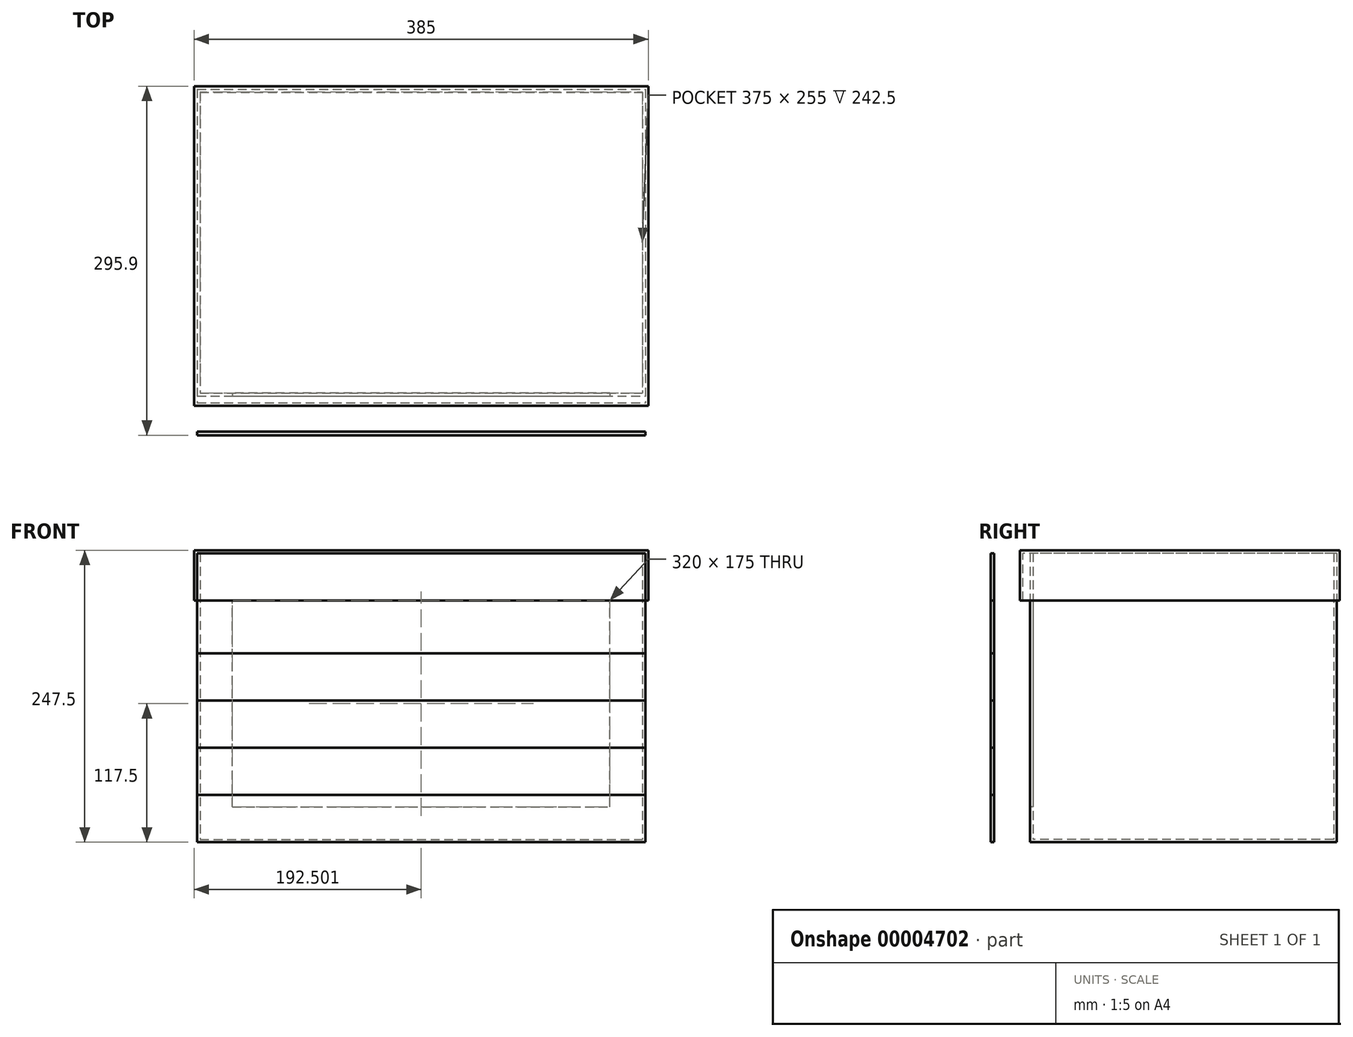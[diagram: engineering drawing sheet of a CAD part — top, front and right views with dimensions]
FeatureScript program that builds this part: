
annotation { "Feature Type Name" : "Feature", "Feature Type Description" : "" }
export const myFeature = defineFeature(function(context is Context, id is Id, definition is map)
    precondition{}
    {
        {
            var Q0;
            Q0=qCreatedBy(makeId("Top.planeOp"),FACE);
            var Q1;
            Q1 = qBodyType(qCreatedBy(id + "F1" ,EDGE), BodyType.WIRE);
            var Q2;
            Q2 = qBodyType(qCreatedBy(id + "F6" ,EDGE), BodyType.WIRE);
            cPlane(context, id + "F0", {"entities" : qUnion([Q0, Q1, Q2]), "cplaneType" : CPlaneType.OFFSET, "offset" : 245 * mm, "width" : 150 * mm, "height" : 150 * mm});
        }
        {
            var Q0;
            Q0=qCreatedBy(makeId("Top.planeOp"),FACE);
            var sketch = newSketch(context, id + "F1", { "sketchPlane" : qUnion([Q0])});
            skLineSegment(sketch, "E0.bottom", {"start": v(-188.2, 120.87) * mm, "end": v(191.8, 120.87) * mm});
            skLineSegment(sketch, "E0.top", {"start": v(-188.2, -139.13) * mm, "end": v(191.8, -139.13) * mm});
            skLineSegment(sketch, "E0.left", {"start": v(-188.2, 120.87) * mm, "end": v(-188.2, -139.13) * mm});
            skLineSegment(sketch, "E0.right", {"start": v(191.8, 120.87) * mm, "end": v(191.8, -139.13) * mm});
            skSolve(sketch);
        }
        {
            var Q0;
            Q0 = qSketchRegion(id + "F1", true);
            var Q1;
            Q1=qCreatedBy(id+"F0.planeOp",FACE);
            extrude(context, id + "F2", {"entities" : qUnion([Q0]), "endBound" : BoundingType.UP_TO_SURFACE, "endBoundEntityFace" : qUnion([Q1]), "depth" : 240 * mm});
        }
        {
            var Q0;
            Q0=makeQuery(id+"F2.opExtrude","CAP_FACE",FACE,{"disambiguationData":[OSD([sQuery(id+"F1.wireOp",EDGE,"E0.bottom"),sQuery(id+"F1.wireOp",EDGE,"E0.top"),sQuery(id+"F1.wireOp",EDGE,"E0.left"),sQuery(id+"F1.wireOp",EDGE,"E0.right")])],"isStart":false});
            shell(context, id + "F3", {"entities" : qUnion([Q0]), "thickness" : 2.5 * mm});
        }
        {
            var Q0;
            Q0=makeQuery(id+"F2.opExtrude","SWEPT_FACE",FACE,{"disambiguationData":[OSD([sQuery(id+"F1.wireOp",EDGE,"E0.top")])]});
            var sketch = newSketch(context, id + "F4", { "sketchPlane" : qUnion([Q0])});
            skLineSegment(sketch, "E1.bottom", {"start": v(-158.2, 30) * mm, "end": v(161.8, 30) * mm});
            skLineSegment(sketch, "E1.top", {"start": v(-158.2, 205) * mm, "end": v(161.8, 205) * mm});
            skLineSegment(sketch, "E1.left", {"start": v(-158.2, 30) * mm, "end": v(-158.2, 205) * mm});
            skLineSegment(sketch, "E1.right", {"start": v(161.8, 30) * mm, "end": v(161.8, 205) * mm});
            skSolve(sketch);
        }
        {
            var Q0;
            Q0 = qSketchRegion(id + "F4", true);
            extrude(context, id + "F5", {"entities" : qUnion([Q0]), "operationType" : NewBodyOperationType.REMOVE, "oppositeDirection" : true, "depth" : 3 * mm});
        }
        {
            var Q0;
            Q0=makeQuery(id+"F2.opExtrude","SWEPT_FACE",FACE,{"disambiguationData":[OSD([sQuery(id+"F1.wireOp",EDGE,"E0.right")])]});
            var sketch = newSketch(context, id + "F6", { "sketchPlane" : qUnion([Q0])});
            skLineSegment(sketch, "E2", {"start": v(-169.53, 205) * mm, "end": v(-169.53, 160) * mm});
            skLineSegment(sketch, "E3", {"start": v(-169.53, 0) * mm, "end": v(-172.53, 0) * mm});
            skLineSegment(sketch, "E4", {"start": v(-172.53, 0) * mm, "end": v(-172.53, 245) * mm});
            skLineSegment(sketch, "E5", {"start": v(-172.53, 245) * mm, "end": v(-169.53, 245) * mm});
            skLineSegment(sketch, "E6", {"start": v(-172.53, 205) * mm, "end": v(-169.53, 205) * mm});
            skLineSegment(sketch, "E7", {"start": v(-172.53, 160) * mm, "end": v(-169.53, 160) * mm});
            skLineSegment(sketch, "E8", {"start": v(-172.53, 120) * mm, "end": v(-169.53, 120) * mm});
            skLineSegment(sketch, "E9", {"start": v(-172.53, 80) * mm, "end": v(-169.53, 80) * mm});
            skLineSegment(sketch, "E10", {"start": v(-172.53, 40) * mm, "end": v(-169.53, 40) * mm});
            skLineSegment(sketch, "E11.trimOffspring", {"start": v(-169.53, 120) * mm, "end": v(-169.53, 80) * mm});
            skLineSegment(sketch, "E12.trimOffspring", {"start": v(-169.53, 40) * mm, "end": v(-169.53, 0) * mm});
            skLineSegment(sketch, "E13", {"start": v(-169.53, 245) * mm, "end": v(-169.53, 205) * mm});
            skLineSegment(sketch, "E14", {"start": v(-169.53, 160) * mm, "end": v(-169.53, 120) * mm});
            skLineSegment(sketch, "E15", {"start": v(-169.53, 80) * mm, "end": v(-169.53, 40) * mm});
            skSolve(sketch);
        }
        {
            var Q0;
            {var subQ2=sQuery(id+"F6.wireOp",EDGE,"E3");Q0=makeQuery(id+"F6.imprint","IMPRINT",FACE,{"disambiguationData":[TD([[makeQuery(id+"F6.imprint","IMPRINT",EDGE,{"derivedFrom":subQ2}),-1.0]])]});}
            var Q1;
            {var subQ1=sQuery(id+"F6.wireOp",EDGE,"E8");Q1=makeQuery(id+"F6.imprint","IMPRINT",FACE,{"disambiguationData":[TD([[makeQuery(id+"F6.imprint","IMPRINT",EDGE,{"derivedFrom":subQ1}),-1.0]])]});}
            var Q2;
            Q2=makeQuery(id+"F6.imprint","IMPRINT",FACE,{"disambiguationData":[TD([[makeQuery(id+"F6.imprint","IMPRINT",EDGE,{"derivedFrom":sQuery(id+"F6.wireOp",EDGE,"E2")}),-1.0]])]});
            extrude(context, id + "F7", {"entities" : qUnion([Q0, Q1, Q2]), "oppositeDirection" : true, "depth" : 380 * mm});
        }
        {
            var Q0;
            {var subQ1=sQuery(id+"F6.wireOp",EDGE,"E9");Q0=makeQuery(id+"F6.imprint","IMPRINT",FACE,{"disambiguationData":[TD([[makeQuery(id+"F6.imprint","IMPRINT",EDGE,{"derivedFrom":subQ1}),-1.0]])]});}
            var Q1;
            {var subQ1=sQuery(id+"F6.wireOp",EDGE,"E7");Q1=makeQuery(id+"F6.imprint","IMPRINT",FACE,{"disambiguationData":[TD([[makeQuery(id+"F6.imprint","IMPRINT",EDGE,{"derivedFrom":subQ1}),-1.0]])]});}
            var Q2;
            {var subQ0=sQuery(id+"F6.wireOp",EDGE,"E5");Q2=makeQuery(id+"F6.imprint","IMPRINT",FACE,{"disambiguationData":[TD([[makeQuery(id+"F6.imprint","IMPRINT",EDGE,{"derivedFrom":subQ0}),-1.0]])]});}
            extrude(context, id + "F8", {"entities" : qUnion([Q0, Q1, Q2]), "oppositeDirection" : true, "depth" : 380 * mm});
        }
        {
            var Q0;
            Q0=makeQuery(id+"F2.opExtrude","CAP_FACE",FACE,{"disambiguationData":[OSD([sQuery(id+"F1.wireOp",EDGE,"E0.bottom"),sQuery(id+"F1.wireOp",EDGE,"E0.top"),sQuery(id+"F1.wireOp",EDGE,"E0.left"),sQuery(id+"F1.wireOp",EDGE,"E0.right")])],"isStart":false});
            var sketch = newSketch(context, id + "F9", { "sketchPlane" : qUnion([Q0])});
            skLineSegment(sketch, "E16.bottom", {"start": v(-188.2, 120.87) * mm, "end": v(191.8, 120.87) * mm});
            skLineSegment(sketch, "E16.top", {"start": v(-188.2, -145.13) * mm, "end": v(191.8, -145.13) * mm});
            skLineSegment(sketch, "E16.left", {"start": v(-188.2, 120.87) * mm, "end": v(-188.2, -145.13) * mm});
            skLineSegment(sketch, "E16.right", {"start": v(191.8, 120.87) * mm, "end": v(191.8, -145.13) * mm});
            skSolve(sketch);
        }
        {
            var Q0;
            Q0 = qSketchRegion(id + "F9", true);
            extrude(context, id + "F10", {"entities" : qUnion([Q0]), "oppositeDirection" : true, "depth" : 40 * mm});
        }
        {
            var Q0;
            Q0=makeQuery(id+"F10.opExtrude","CAP_FACE",FACE,{"disambiguationData":[OSD([sQuery(id+"F9.wireOp",EDGE,"E16.bottom"),sQuery(id+"F9.wireOp",EDGE,"E16.top"),sQuery(id+"F9.wireOp",EDGE,"E16.left"),sQuery(id+"F9.wireOp",EDGE,"E16.right")])],"isStart":false});
            shell(context, id + "F11", {"entities" : qUnion([Q0]), "thickness" : 2.5 * mm, "oppositeDirection" : true});
        }
    });
